# Revit family: MRXBOX-VSC
name_source: partatom
category: Mechanical Equipment
revit_build: Autodesk Revit 2018 (Build: 20170223_1515(x64)
units: mm (PartAtom-declared; Revit-internal decimal feet)

## family parameters
Always vertical = No
Cut with Voids When Loaded = No
OmniClass Number = 23.75.00.00
OmniClass Title = Climate Control (HVAC)
Part Type = Normal
Room Calculation Point = No
Round Connector Dimension = Use Diameter
Shared = No
Work Plane-Based = Yes

## types (1)
- MRXBOX-VSC
    Classification.Uniclass.Pr.Description = Fans
    Classification.Uniclass.Pr.Number = Pr_65_67_29
    Default Elevation = 1219 mm
    Description = Wall mounted LCD visual display control for all MRXBOX-ECO heat recovery units
    Fax Number = +44(0)2920-858-222
    Height = 85 mm
    I&M Manual = http://www.nuaire.info
    IFCExportAs = IfcFanType
    Manufacturer = Nuaire
    Manufacturer Name = Nuaire
    Maximum Ambient Temperature = 40 °C
    Model = MRXBOX-VSC
    Nuaire Model Code = MRXBOX-VSC
    OmniClass Number = 23-33 31 19
    OmniClass Title = Fans
    Postcode = CF83 1NA
    Revit Family Last Revised = 06/11/20
    Telephone Number = +44(0)2920-858-200
    Type Comments = Wall mounted LCD visual display control for all MRXBOX-ECO heat recovery units
    URL = http://www.nuaire.co.uk
    Unit Description = Wall mounted LCD visual display control for all MRXBOX-ECO heat recovery units
    VAT Registration Number = 877308
    Warranty Period = 1 Years
    Weatherproof or Internal Only = Internal
    Weight = 0.25 kg
    Width = 145 mm

## geometry (parser evidence)
native form markers: Blend x15, Sweep x2
no freeform markers — native parametric forms only
